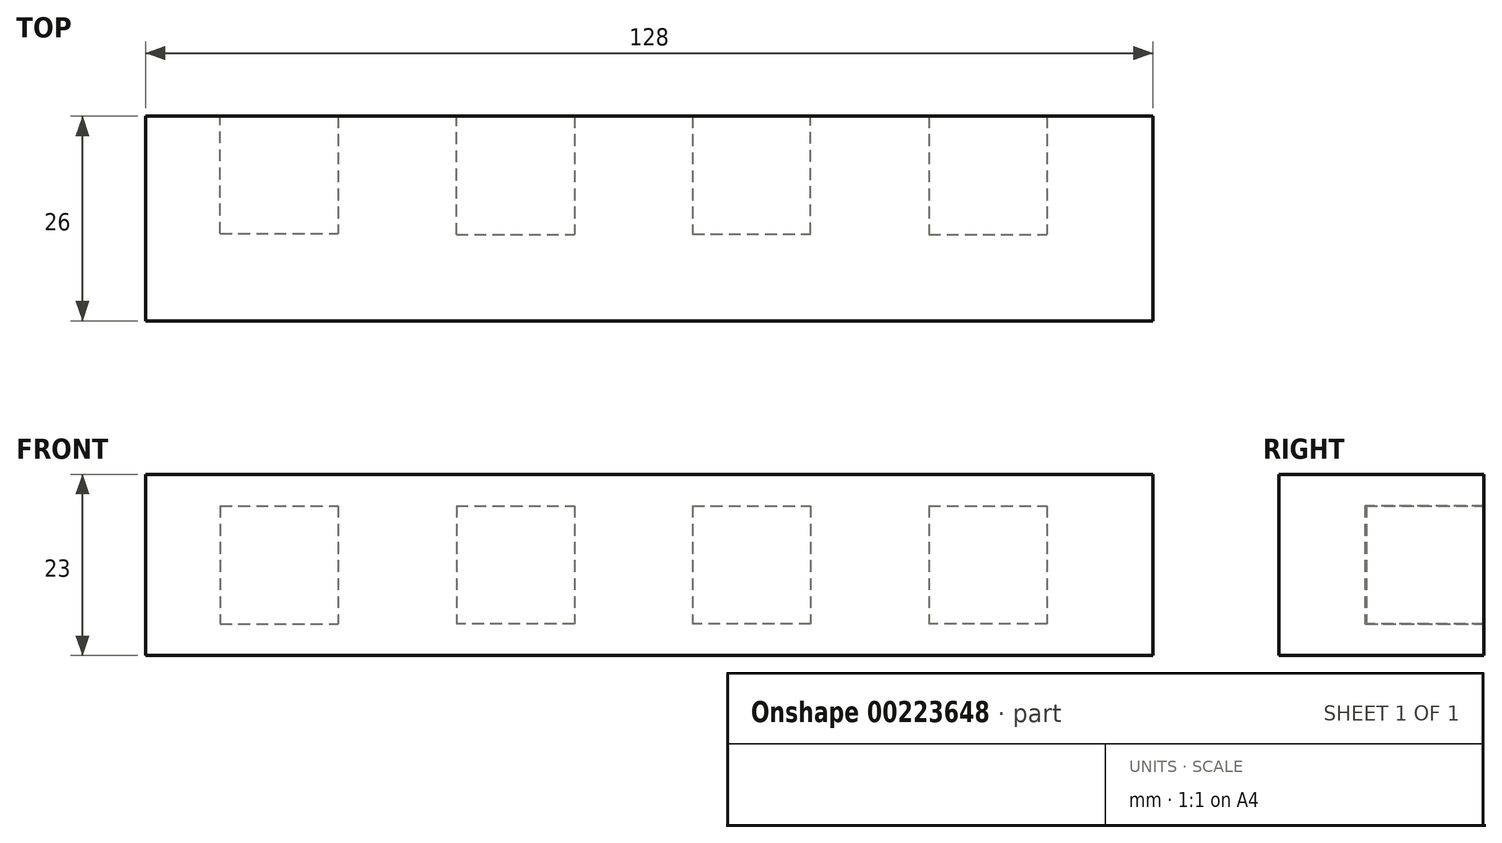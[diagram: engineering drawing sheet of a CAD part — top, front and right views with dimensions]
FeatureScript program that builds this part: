
annotation { "Feature Type Name" : "Feature", "Feature Type Description" : "" }
export const myFeature = defineFeature(function(context is Context, id is Id, definition is map)
    precondition{}
    {
        {
            var Q0;
            Q0=qCreatedBy(makeId("Top.planeOp"),FACE);
            var sketch = newSketch(context, id + "F0", { "sketchPlane" : qUnion([Q0])});
            skLineSegment(sketch, "E0", {"start": v(0, 0) * mm, "end": v(-128, 0) * mm});
            skLineSegment(sketch, "E1", {"start": v(-128, 0) * mm, "end": v(-128, -26) * mm});
            skLineSegment(sketch, "E2", {"start": v(-128, -26) * mm, "end": v(0, -26) * mm});
            skLineSegment(sketch, "E3", {"start": v(0, -26) * mm, "end": v(0, 0) * mm});
            skSolve(sketch);
        }
        {
            var Q0;
            Q0=makeQuery(id+"F0.imprint","IMPRINT",FACE,{"disambiguationData":[TD([[makeQuery(id+"F0.imprint","IMPRINT",EDGE,{"derivedFrom":sQuery(id+"F0.wireOp",EDGE,"E0")}),1.0]])]});
            extrude(context, id + "F1", {"entities" : qUnion([Q0]), "depth" : 4 * mm});
        }
        {
            var Q0;
            Q0=makeQuery(id+"F1.opExtrude","CAP_FACE",FACE,{"disambiguationData":[OSD([sQuery(id+"F0.wireOp",EDGE,"E0"),sQuery(id+"F0.wireOp",EDGE,"E1"),sQuery(id+"F0.wireOp",EDGE,"E2"),sQuery(id+"F0.wireOp",EDGE,"E3")])],"isStart":false});
            var sketch = newSketch(context, id + "F2", { "sketchPlane" : qUnion([Q0])});
            skLineSegment(sketch, "E4", {"start": v(-103.5, 0) * mm, "end": v(-103.5, -14.93) * mm});
            skLineSegment(sketch, "E5", {"start": v(-73.5, 0) * mm, "end": v(-73.5, -15.05) * mm});
            skLineSegment(sketch, "E6", {"start": v(-13.5, 0) * mm, "end": v(-13.5, -15.06) * mm});
            skLineSegment(sketch, "E7", {"start": v(-118.5, -14.93) * mm, "end": v(-103.5, -14.93) * mm});
            skLineSegment(sketch, "E8", {"start": v(-88.5, -15.05) * mm, "end": v(-73.5, -15.05) * mm});
            skLineSegment(sketch, "E9", {"start": v(-58.5, -15) * mm, "end": v(-43.5, -15) * mm});
            skLineSegment(sketch, "E10", {"start": v(-28.5, -15.06) * mm, "end": v(-13.5, -15.06) * mm});
            skLineSegment(sketch, "E11", {"start": v(-73.5, 0) * mm, "end": v(-58.5, 0) * mm});
            skLineSegment(sketch, "E12", {"start": v(-43.5, -15) * mm, "end": v(-43.5, 0) * mm});
            skLineSegment(sketch, "E13", {"start": v(-43.5, 0) * mm, "end": v(-28.5, 0) * mm});
            skLineSegment(sketch, "E14", {"start": v(-28.5, 0) * mm, "end": v(-28.5, -15.06) * mm});
            skLineSegment(sketch, "E15", {"start": v(-58.5, 0) * mm, "end": v(-58.5, -15) * mm});
            skLineSegment(sketch, "E16", {"start": v(-118.5, -14.93) * mm, "end": v(-118.5, 0) * mm});
            skLineSegment(sketch, "E17", {"start": v(-132, 0) * mm, "end": v(-132, -26) * mm});
            skLineSegment(sketch, "E18", {"start": v(0, -26) * mm, "end": v(0, 0) * mm});
            skLineSegment(sketch, "E19", {"start": v(-132, 0) * mm, "end": v(-118.5, 0) * mm});
            skLineSegment(sketch, "E20", {"start": v(-132, -26) * mm, "end": v(0, -26) * mm});
            skLineSegment(sketch, "E21", {"start": v(-88.5, -15.05) * mm, "end": v(-88.5, 0) * mm});
            skLineSegment(sketch, "E22", {"start": v(-88.5, 0) * mm, "end": v(-103.5, 0) * mm});
            skSolve(sketch);
        }
        {
            var Q0;
            Q0 = qSketchRegion(id + "F2", true);
            var Q1;
            Q1=makeQuery(id+"F2.imprint","IMPRINT",FACE,{"disambiguationData":[TD([[makeQuery(id+"F2.imprint","IMPRINT",EDGE,{"derivedFrom":sQuery(id+"F2.wireOp",EDGE,"923bc432-da7d-4379-bb65-e857abf57b83")}),-1.0]])]});
            var Q2;
            Q2=makeQuery(id+"F2.imprint","IMPRINT",FACE,{"disambiguationData":[TD([[makeQuery(id+"F2.imprint","IMPRINT",EDGE,{"derivedFrom":sQuery(id+"F2.wireOp",EDGE,"E5")}),1.0]])]});
            extrude(context, id + "F3", {"entities" : qUnion([Q0, Q1, Q2]), "operationType" : NewBodyOperationType.ADD, "depth" : 15 * mm});
        }
        {
            var Q0;
            Q0=makeQuery(id+"F3.opExtrude","CAP_FACE",FACE,{"disambiguationData":[OSD([sQuery(id+"F2.wireOp",EDGE,"923bc432-da7d-4379-bb65-e857abf57b83"),sQuery(id+"F2.wireOp",EDGE,"E5"),sQuery(id+"F2.wireOp",EDGE,"9cc431c0-3aba-466b-9185-eab08a776cd2"),sQuery(id+"F2.wireOp",EDGE,"934cbda5-51be-4693-bddd-5b4c666d3a3c"),sQuery(id+"F2.wireOp",EDGE,"9fb66b9f-51f0-4a7c-8099-e4b68628778d"),sQuery(id+"F2.wireOp",EDGE,"E6"),sQuery(id+"F2.wireOp",EDGE,"E8"),sQuery(id+"F2.wireOp",EDGE,"E9"),sQuery(id+"F2.wireOp",EDGE,"E10"),sQuery(id+"F2.wireOp",EDGE,"fec2ecbf-cdcd-423a-a4fa-0ac8a78bffb0"),sQuery(id+"F2.wireOp",EDGE,"E11"),sQuery(id+"F2.wireOp",EDGE,"2b9e20e7-8852-4b6e-8ec9-4eec8968ec8b"),sQuery(id+"F2.wireOp",EDGE,"E7"),sQuery(id+"F2.wireOp",EDGE,"E4"),sQuery(id+"F2.wireOp",EDGE,"JhjnRjg5-mCsV-GNdX-RPUB-wNquaUOiuOpt"),sQuery(id+"F2.wireOp",EDGE,"5v8hzlPF-9Z5I-gF1c-dwzE-CAkMEKBeIVVC"),sQuery(id+"F2.wireOp",EDGE,"LarPWVQq-4vM4-ddIq-DcqI-BDpMouEFGcQA"),sQuery(id+"F2.wireOp",EDGE,"LGlM9ZKE-OeQz-b3pI-IHwn-hjCOEuLLfXqr"),sQuery(id+"F2.wireOp",EDGE,"srIj263R-Lc7P-RAWa-YquH-BxqXKjjRhaxO"),sQuery(id+"F2.wireOp",EDGE,"VPgy7qMX-3UvW-ZKCa-OSRY-PrbcHX6Cyqjo")])],"isStart":false});
            var sketch = newSketch(context, id + "F4", { "sketchPlane" : qUnion([Q0])});
            skLineSegment(sketch, "E23", {"start": v(0, 0) * mm, "end": v(0, -26) * mm});
            skLineSegment(sketch, "E24", {"start": v(0, -26) * mm, "end": v(-128, -26) * mm});
            skLineSegment(sketch, "E25", {"start": v(-128, -26) * mm, "end": v(-128, 0) * mm});
            skLineSegment(sketch, "E26", {"start": v(-128, 0) * mm, "end": v(0, 0) * mm});
            skSolve(sketch);
        }
        {
            var Q0;
            Q0 = qSketchRegion(id + "F4", true);
            extrude(context, id + "F5", {"entities" : qUnion([Q0]), "operationType" : NewBodyOperationType.ADD, "depth" : 4 * mm});
        }
    });
